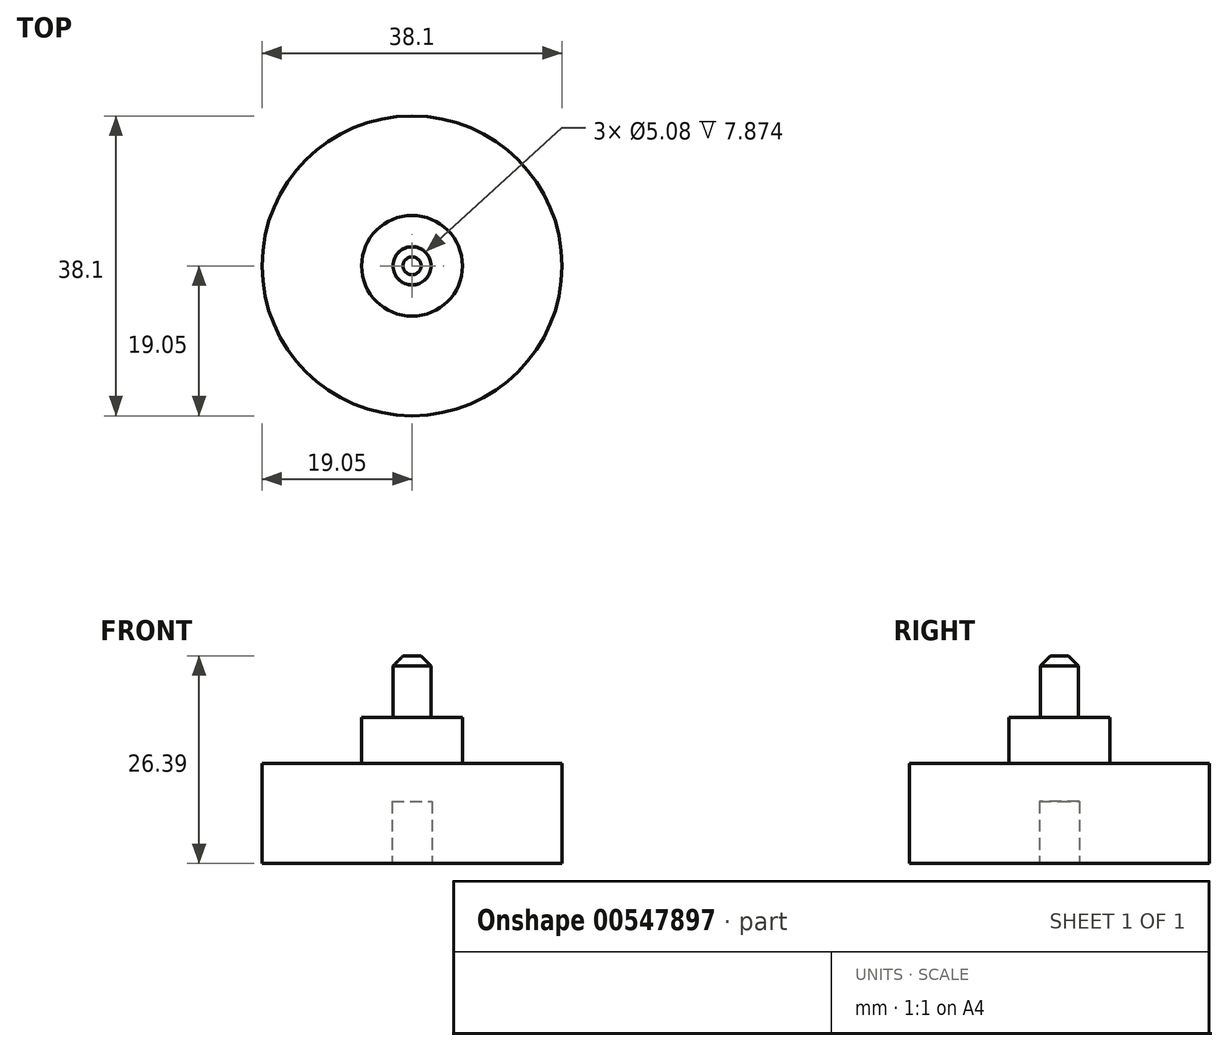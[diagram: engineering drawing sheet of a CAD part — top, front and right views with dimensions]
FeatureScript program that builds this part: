
annotation { "Feature Type Name" : "Feature", "Feature Type Description" : "" }
export const myFeature = defineFeature(function(context is Context, id is Id, definition is map)
    precondition{}
    {
        {
            var Q0;
            Q0=qCreatedBy(makeId("Front.planeOp"),FACE);
            var sketch = newSketch(context, id + "F0", { "sketchPlane" : qUnion([Q0])});
            skLineSegment(sketch, "E0", {"start": v(0, 0) * mm, "end": v(19.05, 0) * mm});
            skLineSegment(sketch, "E1", {"start": v(19.05, 0) * mm, "end": v(19.05, 12.7) * mm});
            skLineSegment(sketch, "E2", {"start": v(19.05, 12.7) * mm, "end": v(6.4, 12.7) * mm});
            skLineSegment(sketch, "E3", {"start": v(2.41, 18.54) * mm, "end": v(6.4, 18.54) * mm});
            skLineSegment(sketch, "E4", {"start": v(6.4, 18.54) * mm, "end": v(6.4, 12.7) * mm});
            skLineSegment(sketch, "E5", {"start": v(0, 26.4) * mm, "end": v(2.41, 26.4) * mm});
            skLineSegment(sketch, "E6", {"start": v(2.41, 26.4) * mm, "end": v(2.41, 18.54) * mm});
            skPoint(sketch, "E7.start.orphan", {"position": v(0, 12.7) * mm});
            skLineSegment(sketch, "E8", {"start": v(2.54, 0) * mm, "end": v(2.54, 7.87) * mm});
            skLineSegment(sketch, "E9", {"start": v(2.54, 7.87) * mm, "end": v(0, 7.87) * mm});
            skLineSegment(sketch, "E10", {"start": v(0, 7.87) * mm, "end": v(0, 26.4) * mm});
            skSolve(sketch);
        }
        {
            var Q0;
            Q0 = qSketchRegion(id + "F0", true);
            var Q1;
            Q1=sQuery(id+"F0.wireOp",EDGE,"E10");
            revolve(context, id + "F1", {"entities" : qUnion([Q0]), "axis" : qUnion([Q1]), "revolveType" : RevolveType.FULL});
        }
        {
            var Q0;
            Q0=makeQuery(id+"F1.opRevolve","SWEPT_EDGE",EDGE,{"disambiguationData":[OSD([sQuery(id+"F0.wireOp",EDGE,"E5"),sQuery(id+"F0.wireOp",EDGE,"E6")])]});
            chamfer(context, id + "F2", {"entities" : qUnion([Q0]), "width" : 1.27 * mm, "tangentPropagation" : true});
        }
    });
